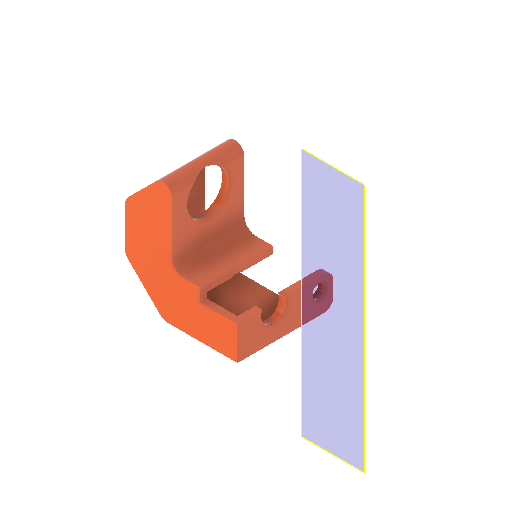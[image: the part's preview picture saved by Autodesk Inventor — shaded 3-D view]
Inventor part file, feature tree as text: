
AUTODESK INVENTOR PART (.ipt)
format: ipt  version: 2022 (Build 260153000, 153)  size: 275,456 bytes
history: native  units: in
note: dims shown in document units (in); Inventor stores cm internally (conversion verified against a paired STEP export)
features: other x8, extrude x7, sketch x6, reference x5, projected_geometry x2, plane x1, fillet x1
ambient origin geometry x8: Origin, YZ Plane, XZ Plane, XY Plane, X Axis, Y Axis, Z Axis, Center Point
bodies: Solid1 (feature_tree)
feature tree (30):
  plane  "Work Plane1"
  extrude  "Extrusion1"  Depth=0.5512in TaperAngle=0.0deg
  extrude  "Extrusion2"  Depth=0.0591in
  extrude  "Extrusion3"  TaperAngle=135.0deg  [1 undecoded]
  extrude  "Extrusion8"  Depth=0.2362in
  extrude  "Extrusion9"  Depth=0.2362in
  extrude  "Extrusion11"  Depth=0.5512in TaperAngle=0.0deg
  extrude  "Extrusion12"  Depth=0.0591in
  fillet  "Rundung1"  Radius=0.0591in
  sketch  "Sketch2"  dims[d0=0.0591in d1=0.0in d3=0.5512in d4=0.0in]
  sketch  "Sketch3"  dims[d12=0.0591in d13=0.0in d22=0.5307in]
  reference  "Reference1"
  projected_geometry  "Projected Loop5"
  projected_geometry  "Projected Loop6"
  sketch  "Sketch8"  dims[d23=0.2653in d25=135.0deg]
  reference  "Reference2"
  reference  "Reference3"
  sketch  "Sketch9"  dims[d26=0.1575in d27=0.2362in]
  reference  "Reference4"
  sketch  "Skizze11"  dims[d28=0.1568in d29=0.2362in]
  sketch  "Skizze12"  dims[d31=0.3937in d35=0.5512in d36=0.0in d40=0.0591in d41=0.0591in d42=0.9449in d43=0.5512in d44=0.0in d45=0.0in d48=0.0in d49=0.0in d50=0.1969in d51=0.3937in d52=0.0in d53=0.0787in]
  reference  "Referenz5"
  other  "<userpath>\Documents\Matchboxscope\INVENTOR\Matchboxscope_v0.iam"
  other  "Matchboxscope_v0.iam"
  other  "Matchboxscope_sample_v0:1"
  other  "Matchboxscope_middle2_v1:1"
  other  "00_ESP3-CAM:5"
  other  "Bauteil50"
  other  "Assembly_Matchboxscope_injectionmolded.iam"
  other  "IM_Matchboxscope_plate:2"
note: 1 required parameter value undecoded (feature->parameter linkage not recoverable at this tier; creation-order binding heuristic only, values carry confidence <= 0.55)
